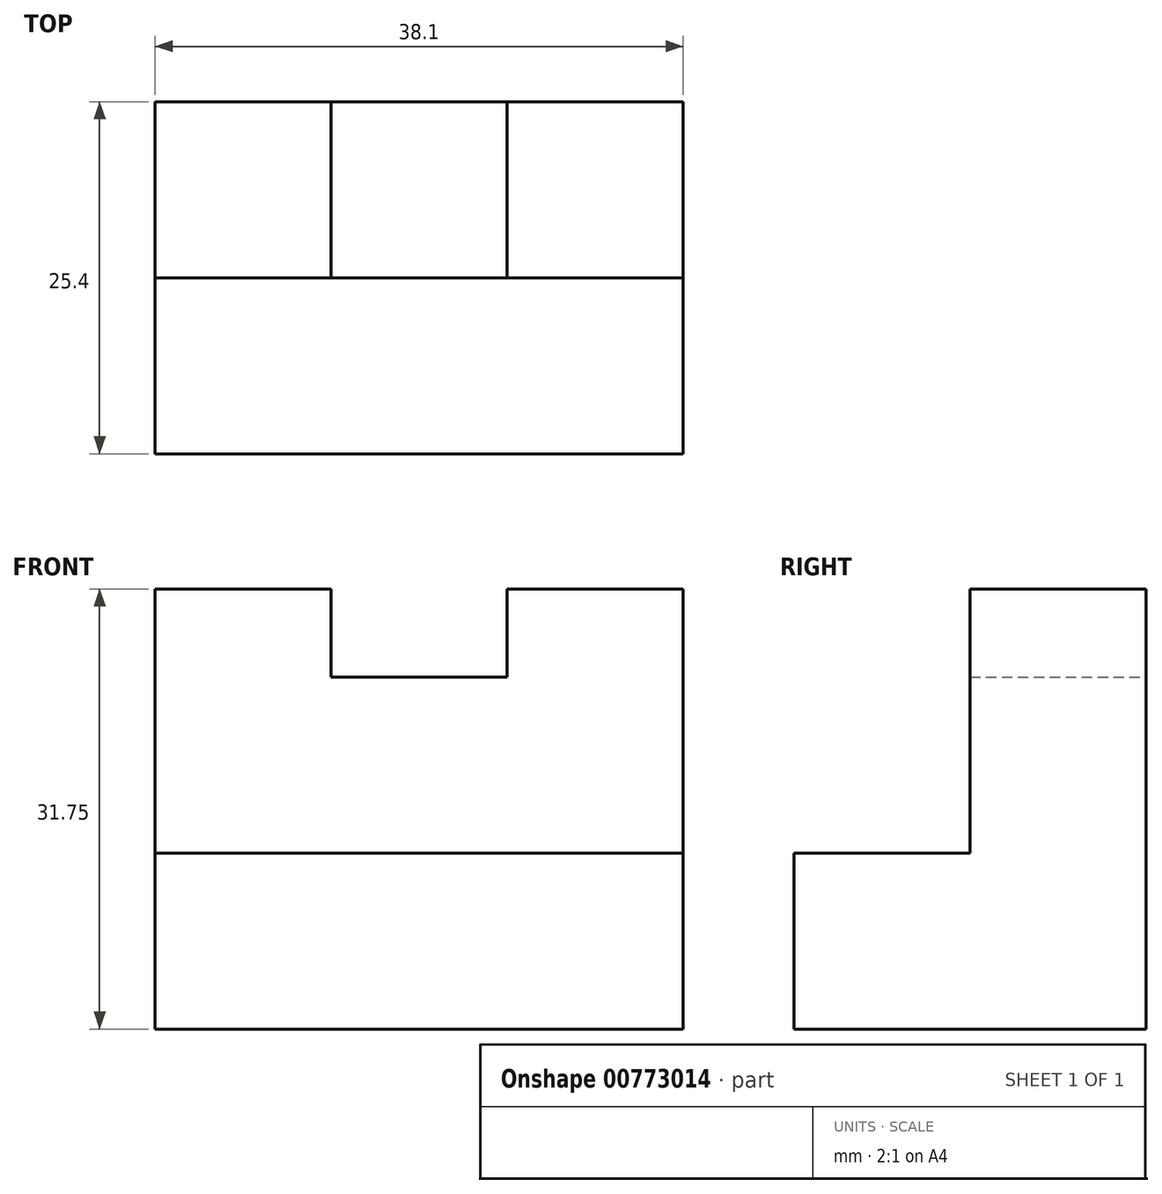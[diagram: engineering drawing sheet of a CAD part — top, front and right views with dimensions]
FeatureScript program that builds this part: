
annotation { "Feature Type Name" : "Feature", "Feature Type Description" : "" }
export const myFeature = defineFeature(function(context is Context, id is Id, definition is map)
    precondition{}
    {
        {
            var Q0;
            Q0=qCreatedBy(makeId("Right.planeOp"),FACE);
            var sketch = newSketch(context, id + "F0", { "sketchPlane" : qUnion([Q0])});
            skLineSegment(sketch, "E0", {"start": v(0, 0) * mm, "end": v(25.4, 0) * mm});
            skLineSegment(sketch, "E1", {"start": v(25.4, 0) * mm, "end": v(25.4, 31.75) * mm});
            skLineSegment(sketch, "E2", {"start": v(25.4, 31.75) * mm, "end": v(19.05, 31.75) * mm});
            skLineSegment(sketch, "E3", {"start": v(19.05, 31.75) * mm, "end": v(19.05, 12.7) * mm});
            skLineSegment(sketch, "E4", {"start": v(19.05, 12.7) * mm, "end": v(0, 12.7) * mm});
            skLineSegment(sketch, "E5", {"start": v(0, 12.7) * mm, "end": v(0, 0) * mm});
            skSolve(sketch);
        }
        {
            var Q0;
            Q0=makeQuery(id+"F0.imprint","IMPRINT",FACE,{"disambiguationData":[TD([[makeQuery(id+"F0.imprint","IMPRINT",EDGE,{"derivedFrom":sQuery(id+"F0.wireOp",EDGE,"E0")}),1.0]])]});
            extrude(context, id + "F1", {"entities" : qUnion([Q0]), "depth" : 38.1 * mm, "offsetDistance" : 25.4 * mm});
        }
        {
            var Q0;
            Q0=makeQuery(id+"F1.opExtrude","SWEPT_FACE",FACE,{"disambiguationData":[OSD([sQuery(id+"F0.wireOp",EDGE,"E3")])]});
            var sketch = newSketch(context, id + "F2", { "sketchPlane" : qUnion([Q0])});
            skLineSegment(sketch, "E6", {"start": v(0, 31.75) * mm, "end": v(12.7, 31.75) * mm});
            skLineSegment(sketch, "E7", {"start": v(12.7, 31.75) * mm, "end": v(12.7, 25.4) * mm});
            skLineSegment(sketch, "E8", {"start": v(12.7, 25.4) * mm, "end": v(25.4, 25.4) * mm});
            skLineSegment(sketch, "E9", {"start": v(25.4, 25.4) * mm, "end": v(25.4, 31.75) * mm});
            skLineSegment(sketch, "E10", {"start": v(25.4, 31.75) * mm, "end": v(38.1, 31.75) * mm});
            skSolve(sketch);
        }
        {
            var Q0;
            Q0=makeQuery(id+"F2.imprint","IMPRINT",FACE,{"disambiguationData":[TD([[makeQuery(id+"F2.imprint","IMPRINT",EDGE,{"derivedFrom":sQuery(id+"F2.wireOp",EDGE,"E6")}),1.0]])]});
            extrude(context, id + "F3", {"entities" : qUnion([Q0]), "operationType" : NewBodyOperationType.ADD, "depth" : 6.35 * mm, "offsetDistance" : 25.4 * mm});
        }
        {
            var Q0;
            Q0=makeQuery(id+"F1.opExtrude","SWEPT_FACE",FACE,{"disambiguationData":[OSD([sQuery(id+"F0.wireOp",EDGE,"E3")])]});
            extrude(context, id + "F4", {"entities" : qUnion([Q0]), "operationType" : NewBodyOperationType.REMOVE, "oppositeDirection" : true, "depth" : 6.35 * mm, "offsetDistance" : 25.4 * mm});
        }
    });
